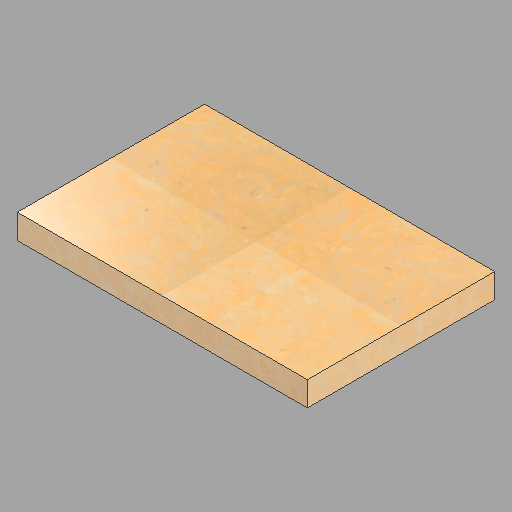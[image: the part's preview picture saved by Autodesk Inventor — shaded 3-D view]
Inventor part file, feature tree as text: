
AUTODESK INVENTOR PART (.ipt)
format: ipt  version: 2022.2 (Build 262287010, 287A)  size: 248,832 bytes
history: native  units: in
note: dims shown in document units (in); Inventor stores cm internally (conversion verified against a paired STEP export)
features: extrude x1, sketch x1
ambient origin geometry x8: Origin, YZ Plane, XZ Plane, XY Plane, X Axis, Y Axis, Z Axis, Center Point
bodies: Solid1 (feature_tree)
feature tree (2):
  extrude  "Extrusion1"  Depth=23.0in
  sketch  "Sketch1"  dims[d0=35.625in d1=23.0in d2=3.0in d3=0.0in]
